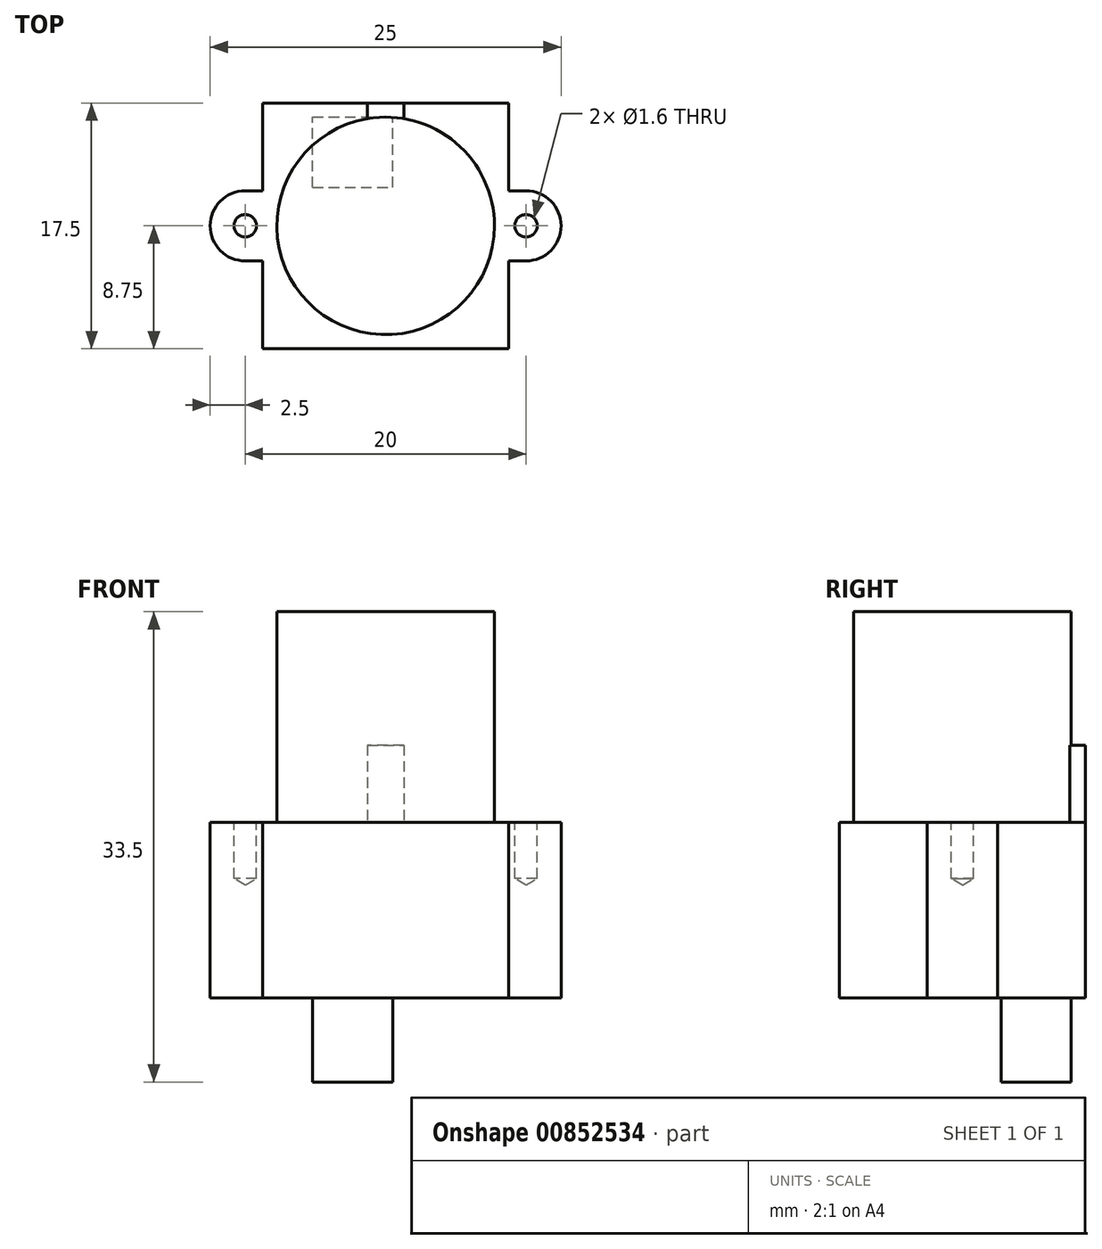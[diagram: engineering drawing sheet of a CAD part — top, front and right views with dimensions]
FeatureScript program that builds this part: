
annotation { "Feature Type Name" : "Feature", "Feature Type Description" : "" }
export const myFeature = defineFeature(function(context is Context, id is Id, definition is map)
    precondition{}
    {
        {
            var Q0;
            Q0=qCreatedBy(makeId("Top.planeOp"),FACE);
            var sketch = newSketch(context, id + "F0", { "sketchPlane" : qUnion([Q0])});
            skLineSegment(sketch, "E0.bottom", {"start": v(8.75, 8.75) * mm, "end": v(-8.75, 8.75) * mm});
            skLineSegment(sketch, "E0.top", {"start": v(8.75, -8.75) * mm, "end": v(-8.75, -8.75) * mm});
            skLineSegment(sketch, "E0.left", {"start": v(8.75, 8.75) * mm, "end": v(8.75, -8.75) * mm});
            skLineSegment(sketch, "E0.right", {"start": v(-8.75, 8.75) * mm, "end": v(-8.75, -8.75) * mm});
            skPoint(sketch, "E0.middle", {"position": v(0, 0) * mm});
            skSolve(sketch);
        }
        {
            var Q0;
            Q0=makeQuery(id+"F0.imprint","IMPRINT",FACE,{"disambiguationData":[TD([[makeQuery(id+"F0.imprint","IMPRINT",EDGE,{"derivedFrom":sQuery(id+"F0.wireOp",EDGE,"E0.bottom")}),1.0]])]});
            extrude(context, id + "F1", {"entities" : qUnion([Q0]), "depth" : 12.5 * mm, "offsetDistance" : 25 * mm, "hasSecondDirectionDraft" : true, "secondDirectionDraftAngle" : 15 * degree});
        }
        {
            var Q0;
            Q0=makeQuery(id+"F1.opExtrude","CAP_FACE",FACE,{"disambiguationData":[OSD([sQuery(id+"F0.wireOp",EDGE,"E0.bottom"),sQuery(id+"F0.wireOp",EDGE,"E0.top"),sQuery(id+"F0.wireOp",EDGE,"E0.left"),sQuery(id+"F0.wireOp",EDGE,"E0.right")])],"isStart":false});
            var sketch = newSketch(context, id + "F2", { "sketchPlane" : qUnion([Q0])});
            skCircle(sketch, "E1", {"center": v(0, 0) * mm, "radius": 7.75 * mm});
            skSolve(sketch);
        }
        {
            var Q0;
            Q0=makeQuery(id+"F2.imprint","IMPRINT",FACE,{"disambiguationData":[TD([[makeQuery(id+"F2.imprint","IMPRINT",EDGE,{"derivedFrom":sQuery(id+"F2.wireOp",EDGE,"E1")}),1.0]])]});
            extrude(context, id + "F3", {"entities" : qUnion([Q0]), "operationType" : NewBodyOperationType.ADD, "depth" : 15 * mm, "offsetDistance" : 25 * mm});
        }
        {
            var Q0;
            Q0=makeQuery(id+"F1.opExtrude","CAP_FACE",FACE,{"disambiguationData":[OSD([sQuery(id+"F0.wireOp",EDGE,"E0.bottom"),sQuery(id+"F0.wireOp",EDGE,"E0.top"),sQuery(id+"F0.wireOp",EDGE,"E0.left"),sQuery(id+"F0.wireOp",EDGE,"E0.right")])],"isStart":false});
            var sketch = newSketch(context, id + "F4", { "sketchPlane" : qUnion([Q0])});
            skArc(sketch, "E2", {"start": v(-10, 2.5) * mm, "mid": v(-12.5, 0) * mm, "end": v(-10, -2.5) * mm});
            skArc(sketch, "E3", {"start": v(10, -2.5) * mm, "mid": v(12.5, 0) * mm, "end": v(10, 2.5) * mm});
            skLineSegment(sketch, "E4", {"start": v(-10, 2.5) * mm, "end": v(10, 2.5) * mm});
            skLineSegment(sketch, "E5", {"start": v(10, -2.5) * mm, "end": v(-10, -2.5) * mm});
            skPoint(sketch, "E6", {"position": v(-12.5, 0) * mm});
            skPoint(sketch, "E7", {"position": v(12.5, 0) * mm});
            skLineSegment(sketch, "E8", {"start": v(-10, 0) * mm, "end": v(10, 0) * mm, "construction": true});
            skSolve(sketch);
        }
        {
            var Q0;
            Q0 = qSketchRegion(id + "F4", true);
            var Q1;
            Q1=makeQuery(id+"F1.opExtrude","CAP_FACE",FACE,{"disambiguationData":[OSD([sQuery(id+"F0.wireOp",EDGE,"E0.bottom"),sQuery(id+"F0.wireOp",EDGE,"E0.top"),sQuery(id+"F0.wireOp",EDGE,"E0.left"),sQuery(id+"F0.wireOp",EDGE,"E0.right")])],"isStart":true});
            extrude(context, id + "F5", {"entities" : qUnion([Q0]), "operationType" : NewBodyOperationType.ADD, "endBound" : BoundingType.UP_TO_SURFACE, "oppositeDirection" : true, "depth" : 25 * mm, "endBoundEntityFace" : qUnion([Q1]), "offsetDistance" : 25 * mm});
        }
        {
            var Q0;
            Q0=sQuery(id+"F4.wireOp",VERTEX,"E8.start");
            var Q1;
            Q1=sQuery(id+"F4.wireOp",VERTEX,"E8.end");
            var Q2;
            Q2=makeQuery(id+"F1.opExtrude","SWEPT_BODY",BODY,{"disambiguationData":[OSD([sQuery(id+"F0.wireOp",EDGE,"E0.bottom"),sQuery(id+"F0.wireOp",EDGE,"E0.top"),sQuery(id+"F0.wireOp",EDGE,"E0.left"),sQuery(id+"F0.wireOp",EDGE,"E0.right")])]});
            hole(context, id + "F6", {"style" : HoleStyle.SIMPLE, "endStyle" : HoleEndStyle.BLIND, "holeDiameter" : 1.6 * mm, "majorDiameter" : 5 * mm, "holeDepth" : 4 * mm, "isTappedThrough" : true, "tappedDepth" : 12 * mm, "tapClearance" : 3, "locations" : qUnion([Q0, Q1]), "scope" : qUnion([Q2])});
        }
        {
            var Q0;
            Q0=qCreatedBy(makeId("Top.planeOp"),FACE);
            var sketch = newSketch(context, id + "F7", { "sketchPlane" : qUnion([Q0])});
            skLineSegment(sketch, "E9.bottom", {"start": v(-5.2, 2.75) * mm, "end": v(0.5, 2.75) * mm});
            skLineSegment(sketch, "E9.top", {"start": v(-5.2, 7.75) * mm, "end": v(0.5, 7.75) * mm});
            skLineSegment(sketch, "E9.left", {"start": v(-5.2, 2.75) * mm, "end": v(-5.2, 7.75) * mm});
            skLineSegment(sketch, "E9.right", {"start": v(0.5, 2.75) * mm, "end": v(0.5, 7.75) * mm});
            skLineSegment(sketch, "E10.0", {"start": v(-8.75, 8.75) * mm, "end": v(-8.75, 2.5) * mm, "construction": true});
            skSolve(sketch);
        }
        {
            var Q0;
            Q0=makeQuery(id+"F7.imprint","IMPRINT",FACE,{"disambiguationData":[TD([[makeQuery(id+"F7.imprint","IMPRINT",EDGE,{"derivedFrom":sQuery(id+"F7.wireOp",EDGE,"E9.bottom")}),1.0]])]});
            extrude(context, id + "F8", {"entities" : qUnion([Q0]), "operationType" : NewBodyOperationType.ADD, "oppositeDirection" : true, "depth" : 6 * mm, "offsetDistance" : 25 * mm});
        }
        {
            var Q0;
            Q0=makeQuery(id+"F1.opExtrude","SWEPT_FACE",FACE,{"disambiguationData":[OSD([sQuery(id+"F0.wireOp",EDGE,"E0.bottom")])]});
            var sketch = newSketch(context, id + "F9", { "sketchPlane" : qUnion([Q0])});
            skLineSegment(sketch, "E11.0", {"start": v(-8.75, 12.5) * mm, "end": v(8.75, 12.5) * mm, "construction": true});
            skLineSegment(sketch, "E12.bottom", {"start": v(-1.3, 18) * mm, "end": v(1.3, 18) * mm});
            skLineSegment(sketch, "E12.left", {"start": v(-1.3, 18) * mm, "end": v(-1.3, 12.5) * mm});
            skLineSegment(sketch, "E12.right", {"start": v(1.3, 18) * mm, "end": v(1.3, 12.5) * mm});
            skPoint(sketch, "E12.middle", {"position": v(0, 12.5) * mm});
            skLineSegment(sketch, "E13", {"start": v(0, 12.5) * mm, "end": v(0, 18) * mm, "construction": true});
            skSolve(sketch);
        }
        {
            var Q0;
            Q0=makeQuery(id+"F9.imprint","IMPRINT",FACE,{"disambiguationData":[TD([[makeQuery(id+"F9.imprint","IMPRINT",EDGE,{"derivedFrom":sQuery(id+"F9.wireOp",EDGE,"E12.bottom")}),-1.0]])]});
            var Q1;
            Q1=makeQuery(id+"F1.opExtrude","SWEPT_BODY",BODY,{"disambiguationData":[OSD([sQuery(id+"F0.wireOp",EDGE,"E0.bottom"),sQuery(id+"F0.wireOp",EDGE,"E0.top"),sQuery(id+"F0.wireOp",EDGE,"E0.left"),sQuery(id+"F0.wireOp",EDGE,"E0.right")])]});
            extrude(context, id + "F10", {"entities" : qUnion([Q0]), "operationType" : NewBodyOperationType.ADD, "endBound" : BoundingType.UP_TO_BODY, "oppositeDirection" : true, "depth" : 25 * mm, "endBoundEntityBody" : qUnion([Q1]), "offsetDistance" : 25 * mm});
        }
    });
